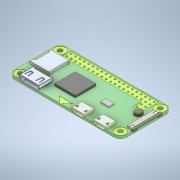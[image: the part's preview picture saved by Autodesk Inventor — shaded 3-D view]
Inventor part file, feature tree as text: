
AUTODESK INVENTOR PART (.ipt)
format: ipt  version: 2020.2 (Build 242310000, 310)  size: 385,536 bytes
history: mixed  units: mm
features: other x1, fillet x1, imported_body x1
ambient origin geometry x8: Origin, YZ Plane, XZ Plane, XY Plane, X Axis, Y Axis, Z Axis, Center Point
bodies: Solid1 (imported_parasolid), Solid2 (imported_parasolid)
feature tree (3):
  other  "Cut-Extrude8"
  fillet  "Fillet3"  [1 undecoded]
  imported_body  NMx_Import_Brep_tag  [imported B-rep: ~316 faces, bbox_mm=[65.9, 4.8, 31.25]]
note: 1 required parameter value undecoded (feature->parameter linkage not recoverable at this tier; creation-order binding heuristic only, values carry confidence <= 0.55)
